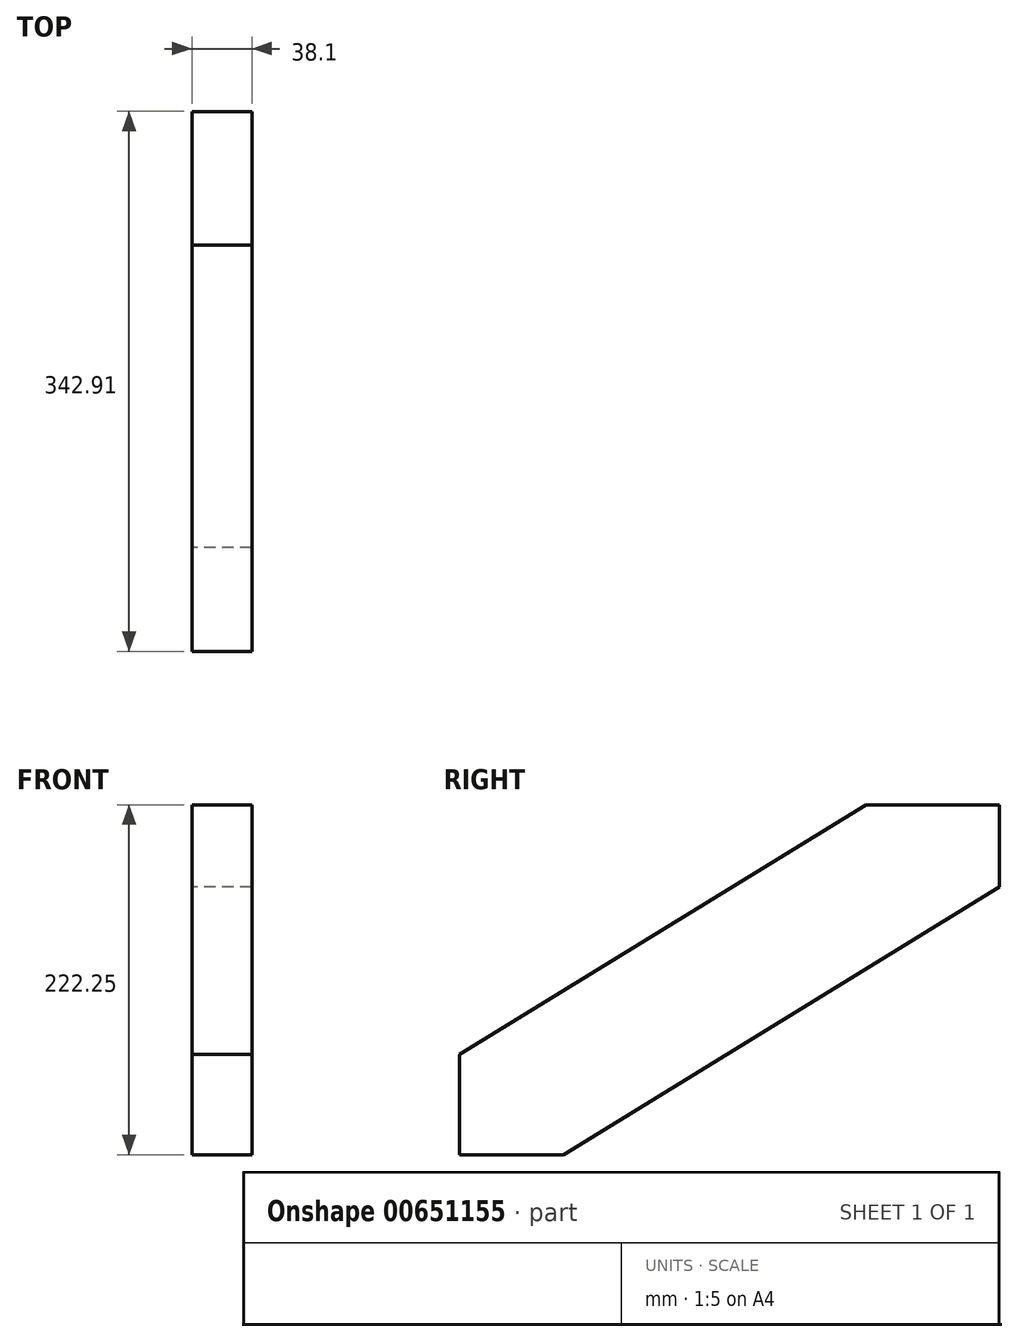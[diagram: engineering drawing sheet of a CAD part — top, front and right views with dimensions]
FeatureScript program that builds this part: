
annotation { "Feature Type Name" : "Feature", "Feature Type Description" : "" }
export const myFeature = defineFeature(function(context is Context, id is Id, definition is map)
    precondition{}
    {
        {
            var Q0;
            Q0=qCreatedBy(makeId("Right.planeOp"),FACE);
            var sketch = newSketch(context, id + "F0", { "sketchPlane" : qUnion([Q0])});
            skPoint(sketch, "E0.middle", {"position": v(0, 0) * mm});
            skLineSegment(sketch, "E1.0", {"start": v(96.03, 111.13) * mm, "end": v(-161.92, -47.27) * mm});
            skLineSegment(sketch, "E2.0", {"start": v(180.98, 58.96) * mm, "end": v(-96.03, -111.13) * mm});
            skLineSegment(sketch, "E3", {"start": v(180.98, 111.13) * mm, "end": v(180.98, 58.96) * mm});
            skLineSegment(sketch, "E4", {"start": v(180.98, 111.13) * mm, "end": v(96.03, 111.12) * mm});
            skLineSegment(sketch, "E5", {"start": v(-161.92, -111.13) * mm, "end": v(-96.03, -111.13) * mm});
            skLineSegment(sketch, "E6", {"start": v(-161.92, -47.27) * mm, "end": v(-161.92, -111.13) * mm});
            skSolve(sketch);
        }
        {
            var Q0;
            Q0=makeQuery(id+"F0.imprint","IMPRINT",FACE,{"disambiguationData":[TD([[makeQuery(id+"F0.imprint","IMPRINT",EDGE,{"derivedFrom":sQuery(id+"F0.wireOp",EDGE,"E1.0")}),1.0]])]});
            extrude(context, id + "F1", {"entities" : qUnion([Q0]), "endBound" : BoundingType.SYMMETRIC, "depth" : 38.1 * mm, "offsetDistance" : 25.4 * mm});
        }
    });
